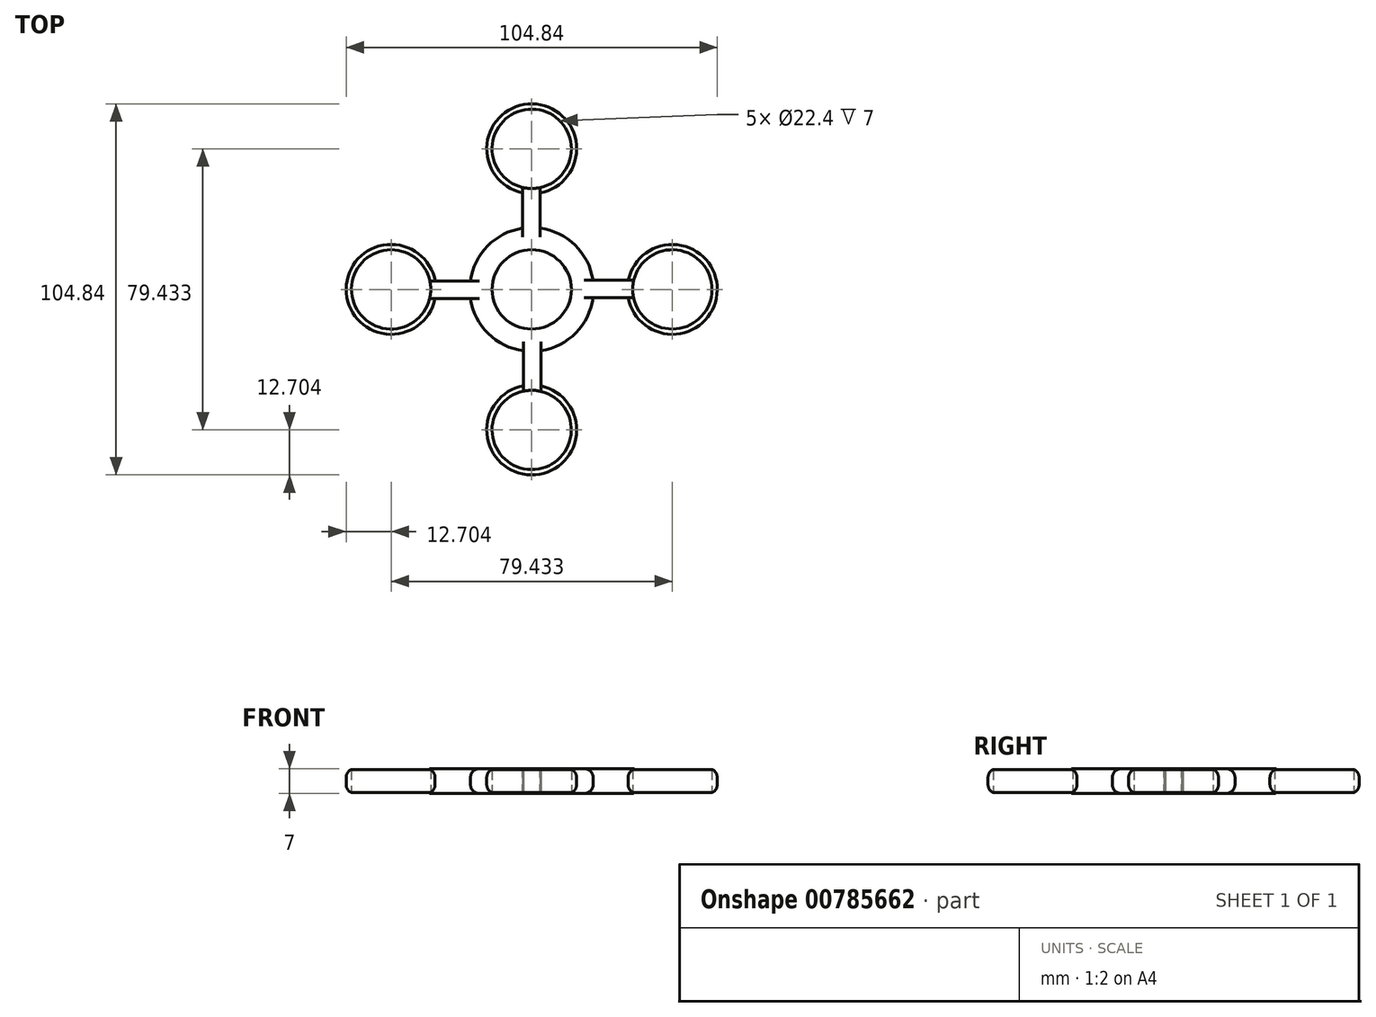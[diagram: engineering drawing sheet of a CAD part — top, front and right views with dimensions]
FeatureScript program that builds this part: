
annotation { "Feature Type Name" : "Feature", "Feature Type Description" : "" }
export const myFeature = defineFeature(function(context is Context, id is Id, definition is map)
    precondition{}
    {
        {
            var Q0;
            Q0=qCreatedBy(makeId("Top.planeOp"),FACE);
            var sketch = newSketch(context, id + "F0", { "sketchPlane" : qUnion([Q0])});
            skCircle(sketch, "E0", {"center": v(0, 0) * mm, "radius": 17.5 * mm});
            skCircle(sketch, "E1", {"center": v(0, 0) * mm, "radius": 11.2 * mm});
            skLineSegment(sketch, "E2", {"start": v(-2.62, 17.3) * mm, "end": v(-2.62, 27.3) * mm});
            skLineSegment(sketch, "E3", {"start": v(2.32, 17.35) * mm, "end": v(2.32, 27.35) * mm});
            skCircle(sketch, "E4", {"center": v(0, 39.72) * mm, "radius": 12.7 * mm});
            skCircle(sketch, "E5", {"center": v(0, 39.72) * mm, "radius": 11.2 * mm});
            skCircle(sketch, "E6.1.0", {"center": v(-39.72, 0) * mm, "radius": 12.7 * mm});
            skCircle(sketch, "E6.1.1", {"center": v(-39.72, 0) * mm, "radius": 11.2 * mm});
            skLineSegment(sketch, "E6.1.2", {"start": v(-17.35, 2.32) * mm, "end": v(-27.35, 2.32) * mm});
            skLineSegment(sketch, "E6.1.3", {"start": v(-17.3, -2.62) * mm, "end": v(-27.3, -2.62) * mm});
            skCircle(sketch, "E6.2.0", {"center": v(0, -39.72) * mm, "radius": 12.7 * mm});
            skCircle(sketch, "E6.2.1", {"center": v(0, -39.72) * mm, "radius": 11.2 * mm});
            skLineSegment(sketch, "E6.2.2", {"start": v(-2.32, -17.35) * mm, "end": v(-2.32, -27.35) * mm});
            skLineSegment(sketch, "E6.2.3", {"start": v(2.62, -17.3) * mm, "end": v(2.62, -27.3) * mm});
            skCircle(sketch, "E7.1.3.0", {"center": v(39.72, 0) * mm, "radius": 12.7 * mm});
            skCircle(sketch, "E7.2.3.0", {"center": v(39.72, 0) * mm, "radius": 11.2 * mm});
            skLineSegment(sketch, "E7.4.3.0", {"start": v(17.35, -2.32) * mm, "end": v(27.35, -2.32) * mm});
            skLineSegment(sketch, "E7.7.3.0", {"start": v(17.3, 2.62) * mm, "end": v(27.3, 2.62) * mm});
            skSolve(sketch);
        }
        {
            var Q0;
            Q0 = qSketchRegion(id + "F0", true);
            extrude(context, id + "F1", {"entities" : qUnion([Q0]), "depth" : 7 * mm, "offsetDistance" : 25 * mm});
        }
        {
            var Q0;
            Q0=makeQuery(id+"F1.opExtrude","CAP_EDGE",EDGE,{"disambiguationData":[OSD([sQuery(id+"F0.wireOp",EDGE,"E6.2.0")])],"isStart":true});
            var Q1;
            Q1=makeQuery(id+"F1.opExtrude","CAP_EDGE",EDGE,{"disambiguationData":[OSD([sQuery(id+"F0.wireOp",EDGE,"E7.1.3.0")])],"isStart":true});
            var Q2;
            Q2=makeQuery(id+"F1.opExtrude","CAP_EDGE",EDGE,{"disambiguationData":[OSD([sQuery(id+"F0.wireOp",EDGE,"E4")])],"isStart":true});
            var Q3;
            Q3=makeQuery(id+"F1.opExtrude","CAP_EDGE",EDGE,{"disambiguationData":[OSD([sQuery(id+"F0.wireOp",EDGE,"E6.1.0")])],"isStart":true});
            var Q4;
            {var subQ0=sQuery(id+"F0.wireOp",EDGE,"E0");Q4=makeQuery(id+"F1.opExtrude","CAP_EDGE",EDGE,{"disambiguationData":[OSD([subQ0]),TDD([makeQuery(id+"F0.imprint","IMPRINT",EDGE,{"disambiguationData":[TD([[makeQuery(id+"F0.imprint","INTERSECT",VERTEX,{"derivedFrom":[subQ0,sQuery(id+"F0.wireOp",EDGE,"E6.1.3")]}),-1.0]])],"derivedFrom":subQ0})])],"isStart":true});}
            var Q5;
            {var subQ0=sQuery(id+"F0.wireOp",EDGE,"E0");Q5=makeQuery(id+"F1.opExtrude","CAP_EDGE",EDGE,{"disambiguationData":[OSD([subQ0]),TDD([makeQuery(id+"F0.imprint","IMPRINT",EDGE,{"disambiguationData":[TD([[makeQuery(id+"F0.imprint","INTERSECT",VERTEX,{"derivedFrom":[subQ0,sQuery(id+"F0.wireOp",EDGE,"E2")]}),-1.0]])],"derivedFrom":subQ0})])],"isStart":true});}
            var Q6;
            {var subQ0=sQuery(id+"F0.wireOp",EDGE,"E0");Q6=makeQuery(id+"F1.opExtrude","CAP_EDGE",EDGE,{"disambiguationData":[OSD([subQ0]),TDD([makeQuery(id+"F0.imprint","IMPRINT",EDGE,{"disambiguationData":[TD([[makeQuery(id+"F0.imprint","INTERSECT",VERTEX,{"derivedFrom":[subQ0,sQuery(id+"F0.wireOp",EDGE,"E3")]}),1.0]])],"derivedFrom":subQ0})])],"isStart":true});}
            var Q7;
            {var subQ0=sQuery(id+"F0.wireOp",EDGE,"E0");Q7=makeQuery(id+"F1.opExtrude","CAP_EDGE",EDGE,{"disambiguationData":[OSD([subQ0]),TDD([makeQuery(id+"F0.imprint","IMPRINT",EDGE,{"disambiguationData":[TD([[makeQuery(id+"F0.imprint","INTERSECT",VERTEX,{"derivedFrom":[subQ0,sQuery(id+"F0.wireOp",EDGE,"E6.2.3")]}),-1.0]])],"derivedFrom":subQ0})])],"isStart":true});}
            fillet(context, id + "F2", {"entities" : qUnion([Q0, Q1, Q2, Q3, Q4, Q5, Q6, Q7]), "radius" : 2.5 * mm, "tangentPropagation" : true, "allowEdgeOverflow" : false});
        }
        {
            var Q0;
            Q0=makeQuery(id+"F1.opExtrude","CAP_EDGE",EDGE,{"disambiguationData":[OSD([sQuery(id+"F0.wireOp",EDGE,"E4")])],"isStart":false});
            var Q1;
            Q1=makeQuery(id+"F1.opExtrude","CAP_EDGE",EDGE,{"disambiguationData":[OSD([sQuery(id+"F0.wireOp",EDGE,"E7.1.3.0")])],"isStart":false});
            var Q2;
            Q2=makeQuery(id+"F1.opExtrude","CAP_EDGE",EDGE,{"disambiguationData":[OSD([sQuery(id+"F0.wireOp",EDGE,"E6.2.0")])],"isStart":false});
            var Q3;
            Q3=makeQuery(id+"F1.opExtrude","CAP_EDGE",EDGE,{"disambiguationData":[OSD([sQuery(id+"F0.wireOp",EDGE,"E6.1.0")])],"isStart":false});
            var Q4;
            {var subQ0=sQuery(id+"F0.wireOp",EDGE,"E0");Q4=makeQuery(id+"F1.opExtrude","CAP_EDGE",EDGE,{"disambiguationData":[OSD([subQ0]),TDD([makeQuery(id+"F0.imprint","IMPRINT",EDGE,{"disambiguationData":[TD([[makeQuery(id+"F0.imprint","INTERSECT",VERTEX,{"derivedFrom":[subQ0,sQuery(id+"F0.wireOp",EDGE,"E6.1.3")]}),-1.0]])],"derivedFrom":subQ0})])],"isStart":false});}
            var Q5;
            {var subQ0=sQuery(id+"F0.wireOp",EDGE,"E0");Q5=makeQuery(id+"F1.opExtrude","CAP_EDGE",EDGE,{"disambiguationData":[OSD([subQ0]),TDD([makeQuery(id+"F0.imprint","IMPRINT",EDGE,{"disambiguationData":[TD([[makeQuery(id+"F0.imprint","INTERSECT",VERTEX,{"derivedFrom":[subQ0,sQuery(id+"F0.wireOp",EDGE,"E2")]}),-1.0]])],"derivedFrom":subQ0})])],"isStart":false});}
            var Q6;
            {var subQ0=sQuery(id+"F0.wireOp",EDGE,"E0");Q6=makeQuery(id+"F1.opExtrude","CAP_EDGE",EDGE,{"disambiguationData":[OSD([subQ0]),TDD([makeQuery(id+"F0.imprint","IMPRINT",EDGE,{"disambiguationData":[TD([[makeQuery(id+"F0.imprint","INTERSECT",VERTEX,{"derivedFrom":[subQ0,sQuery(id+"F0.wireOp",EDGE,"E3")]}),1.0]])],"derivedFrom":subQ0})])],"isStart":false});}
            var Q7;
            {var subQ0=sQuery(id+"F0.wireOp",EDGE,"E0");Q7=makeQuery(id+"F1.opExtrude","CAP_EDGE",EDGE,{"disambiguationData":[OSD([subQ0]),TDD([makeQuery(id+"F0.imprint","IMPRINT",EDGE,{"disambiguationData":[TD([[makeQuery(id+"F0.imprint","INTERSECT",VERTEX,{"derivedFrom":[subQ0,sQuery(id+"F0.wireOp",EDGE,"E6.2.3")]}),-1.0]])],"derivedFrom":subQ0})])],"isStart":false});}
            fillet(context, id + "F3", {"entities" : qUnion([Q0, Q1, Q2, Q3, Q4, Q5, Q6, Q7]), "radius" : 2.5 * mm, "tangentPropagation" : true, "allowEdgeOverflow" : false});
        }
    });
